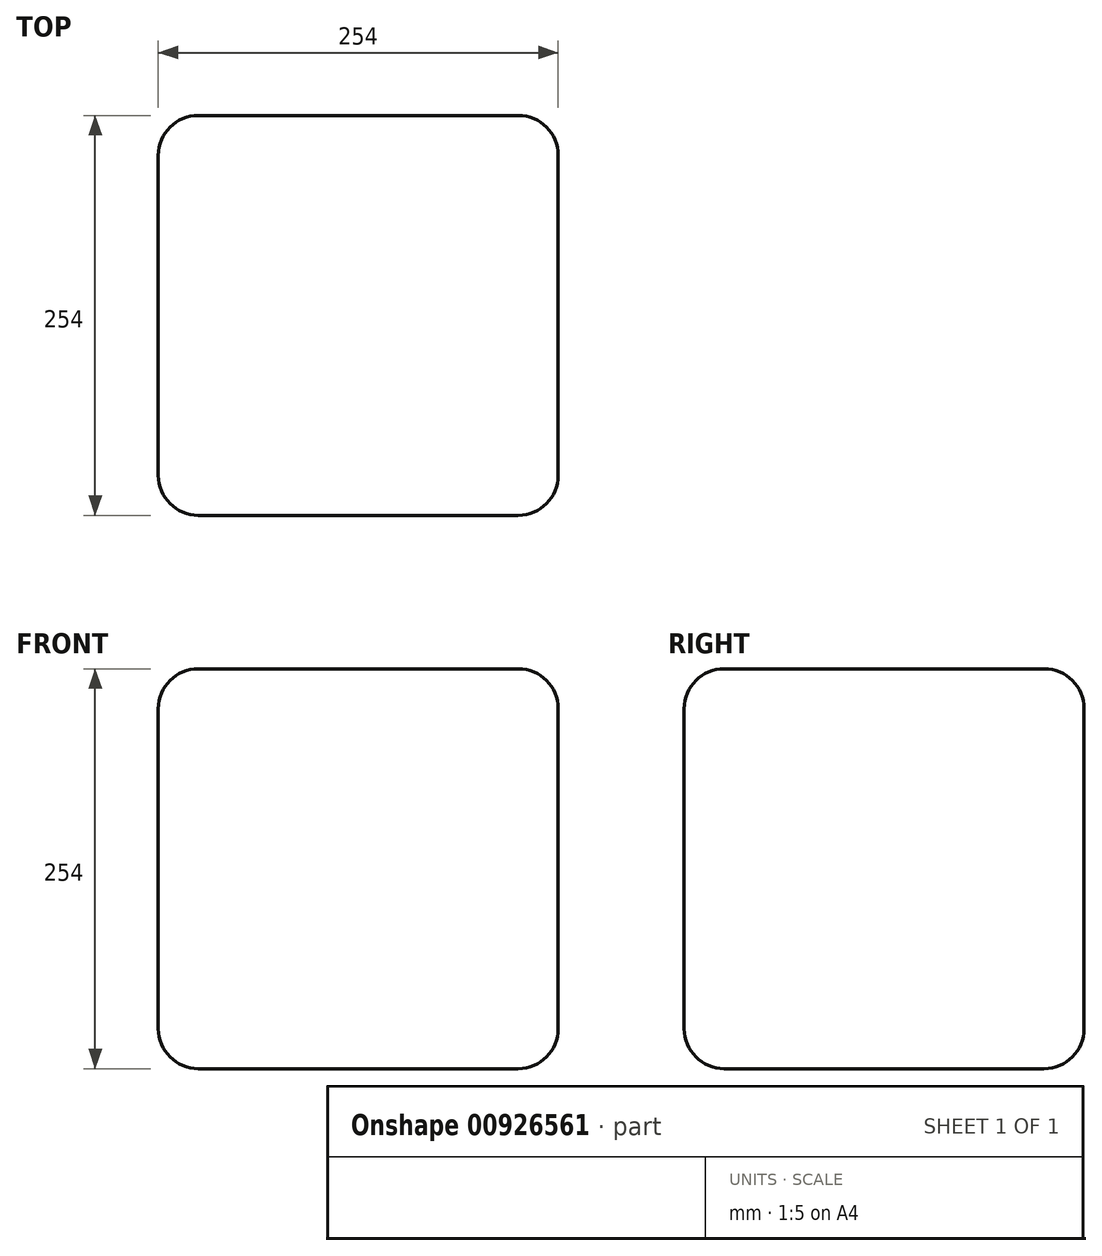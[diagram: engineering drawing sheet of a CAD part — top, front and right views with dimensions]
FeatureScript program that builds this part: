
annotation { "Feature Type Name" : "Feature", "Feature Type Description" : "" }
export const myFeature = defineFeature(function(context is Context, id is Id, definition is map)
    precondition{}
    {
        {
            var Q0;
            Q0=qCreatedBy(makeId("Front.planeOp"),FACE);
            var sketch = newSketch(context, id + "F0", { "sketchPlane" : qUnion([Q0])});
            skLineSegment(sketch, "E0.bottom", {"start": v(-127, 127) * mm, "end": v(127, 127) * mm});
            skLineSegment(sketch, "E0.top", {"start": v(-127, -127) * mm, "end": v(127, -127) * mm});
            skLineSegment(sketch, "E0.left", {"start": v(-127, 127) * mm, "end": v(-127, -127) * mm});
            skLineSegment(sketch, "E0.right", {"start": v(127, 127) * mm, "end": v(127, -127) * mm});
            skPoint(sketch, "E0.middle", {"position": v(0, 0) * mm});
            skSolve(sketch);
        }
        {
            var Q0;
            Q0 = qSketchRegion(id + "F0", true);
            extrude(context, id + "F1", {"entities" : qUnion([Q0]), "depth" : 254 * mm, "offsetDistance" : 25.4 * mm});
        }
        {
            var Q0;
            Q0=makeQuery(id+"F1.opExtrude","CAP_FACE",FACE,{"disambiguationData":[OSD([sQuery(id+"F0.wireOp",EDGE,"E0.bottom"),sQuery(id+"F0.wireOp",EDGE,"E0.top"),sQuery(id+"F0.wireOp",EDGE,"E0.left"),sQuery(id+"F0.wireOp",EDGE,"E0.right")])],"isStart":false});
            var sketch = newSketch(context, id + "F2", { "sketchPlane" : qUnion([Q0])});
            skLineSegment(sketch, "E1", {"start": v(0, 127) * mm, "end": v(0, -127) * mm, "construction": true});
            skLineSegment(sketch, "E2", {"start": v(-127, 0) * mm, "end": v(127, 0) * mm, "construction": true});
            skLineSegment(sketch, "E3", {"start": v(127, 0) * mm, "end": v(127, 63.5) * mm, "construction": true});
            skLineSegment(sketch, "E4", {"start": v(127, 63.5) * mm, "end": v(-127, 63.5) * mm, "construction": true});
            skLineSegment(sketch, "E5", {"start": v(127, 0) * mm, "end": v(127, -63.5) * mm, "construction": true});
            skLineSegment(sketch, "E6", {"start": v(127, -63.5) * mm, "end": v(-127, -63.5) * mm, "construction": true});
            skLineSegment(sketch, "E7", {"start": v(0, 127) * mm, "end": v(-63.5, 127) * mm, "construction": true});
            skLineSegment(sketch, "E8", {"start": v(-63.5, 127) * mm, "end": v(-63.5, -127) * mm, "construction": true});
            skLineSegment(sketch, "E9", {"start": v(0, 127) * mm, "end": v(63.5, 127) * mm, "construction": true});
            skLineSegment(sketch, "E10", {"start": v(63.5, 127) * mm, "end": v(63.5, -127) * mm, "construction": true});
            skSolve(sketch);
        }
        {
            var Q0;
            Q0=makeQuery(id+"F1.opExtrude","CAP_EDGE",EDGE,{"disambiguationData":[OSD([sQuery(id+"F0.wireOp",EDGE,"E0.left")])],"isStart":false});
            var Q1;
            Q1=makeQuery(id+"F1.opExtrude","CAP_EDGE",EDGE,{"disambiguationData":[OSD([sQuery(id+"F0.wireOp",EDGE,"E0.bottom")])],"isStart":false});
            var Q2;
            Q2=makeQuery(id+"F1.opExtrude","CAP_EDGE",EDGE,{"disambiguationData":[OSD([sQuery(id+"F0.wireOp",EDGE,"E0.right")])],"isStart":false});
            var Q3;
            Q3=makeQuery(id+"F1.opExtrude","CAP_EDGE",EDGE,{"disambiguationData":[OSD([sQuery(id+"F0.wireOp",EDGE,"E0.top")])],"isStart":false});
            var Q4;
            Q4=makeQuery(id+"F1.opExtrude","SWEPT_EDGE",EDGE,{"disambiguationData":[OSD([sQuery(id+"F0.wireOp",EDGE,"E0.bottom"),sQuery(id+"F0.wireOp",EDGE,"E0.left")])]});
            var Q5;
            Q5=makeQuery(id+"F1.opExtrude","CAP_EDGE",EDGE,{"disambiguationData":[OSD([sQuery(id+"F0.wireOp",EDGE,"E0.left")])],"isStart":true});
            var Q6;
            Q6=makeQuery(id+"F1.opExtrude","SWEPT_EDGE",EDGE,{"disambiguationData":[OSD([sQuery(id+"F0.wireOp",EDGE,"E0.top"),sQuery(id+"F0.wireOp",EDGE,"E0.left")])]});
            var Q7;
            Q7=makeQuery(id+"F1.opExtrude","CAP_EDGE",EDGE,{"disambiguationData":[OSD([sQuery(id+"F0.wireOp",EDGE,"E0.top")])],"isStart":true});
            var Q8;
            Q8=makeQuery(id+"F1.opExtrude","SWEPT_EDGE",EDGE,{"disambiguationData":[OSD([sQuery(id+"F0.wireOp",EDGE,"E0.top"),sQuery(id+"F0.wireOp",EDGE,"E0.right")])]});
            var Q9;
            Q9=makeQuery(id+"F1.opExtrude","CAP_EDGE",EDGE,{"disambiguationData":[OSD([sQuery(id+"F0.wireOp",EDGE,"E0.right")])],"isStart":true});
            var Q10;
            Q10=makeQuery(id+"F1.opExtrude","SWEPT_EDGE",EDGE,{"disambiguationData":[OSD([sQuery(id+"F0.wireOp",EDGE,"E0.bottom"),sQuery(id+"F0.wireOp",EDGE,"E0.right")])]});
            var Q11;
            Q11=makeQuery(id+"F1.opExtrude","CAP_EDGE",EDGE,{"disambiguationData":[OSD([sQuery(id+"F0.wireOp",EDGE,"E0.bottom")])],"isStart":true});
            fillet(context, id + "F3", {"entities" : qUnion([Q0, Q1, Q2, Q3, Q4, Q5, Q6, Q7, Q8, Q9, Q10, Q11]), "radius" : 25.4 * mm, "tangentPropagation" : true, "allowEdgeOverflow" : false});
        }
    });
